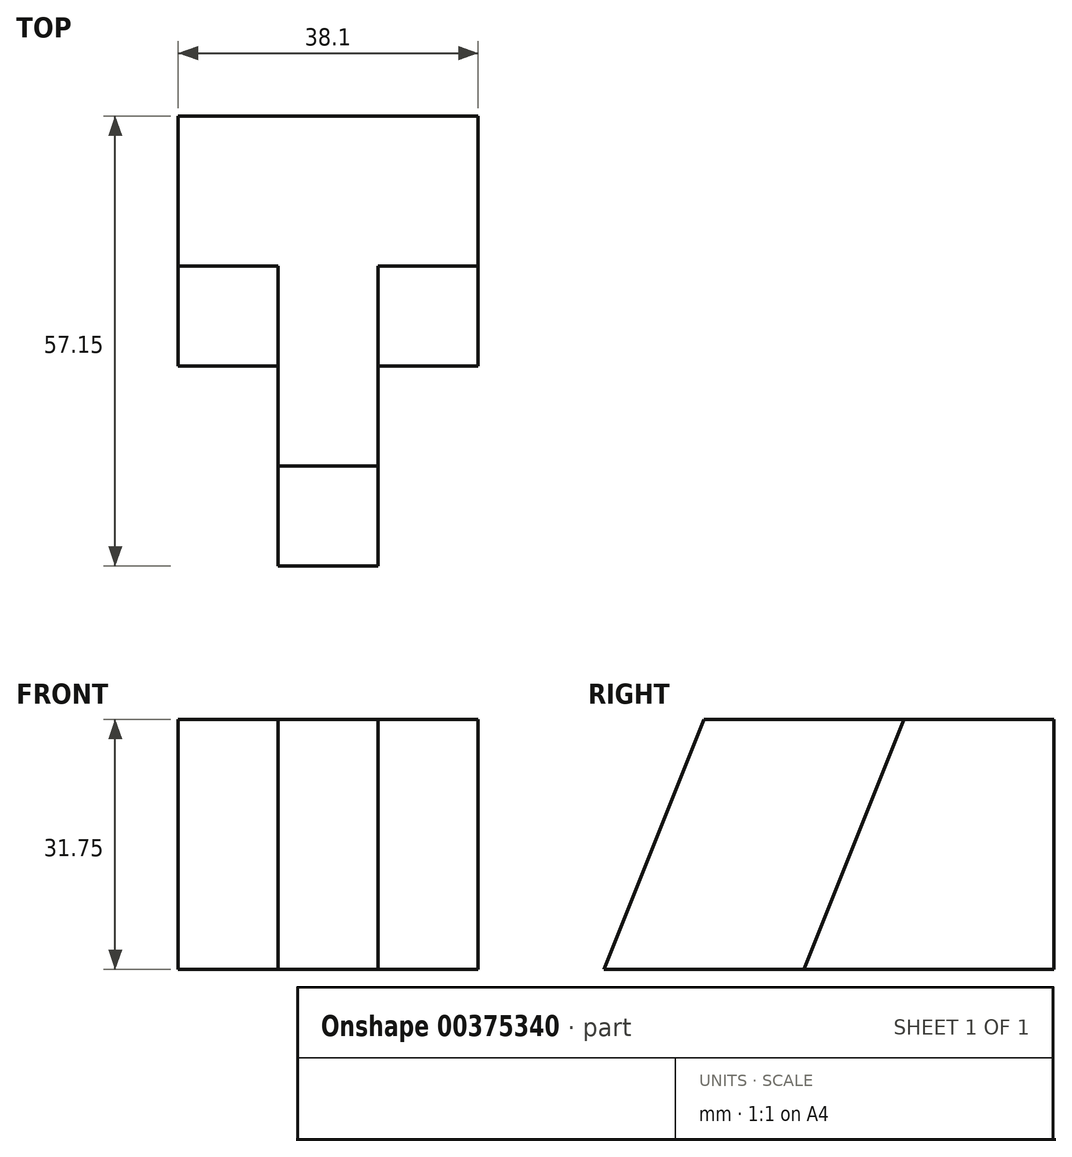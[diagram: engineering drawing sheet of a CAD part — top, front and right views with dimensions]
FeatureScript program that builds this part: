
annotation { "Feature Type Name" : "Feature", "Feature Type Description" : "" }
export const myFeature = defineFeature(function(context is Context, id is Id, definition is map)
    precondition{}
    {
        {
            var Q0;
            Q0=qCreatedBy(makeId("Top.planeOp"),FACE);
            var sketch = newSketch(context, id + "F0", { "sketchPlane" : qUnion([Q0])});
            skLineSegment(sketch, "E0", {"start": v(0, 0) * mm, "end": v(0, -19.05) * mm});
            skLineSegment(sketch, "E1", {"start": v(0, -19.05) * mm, "end": v(12.7, -19.05) * mm});
            skLineSegment(sketch, "E2", {"start": v(12.7, -19.05) * mm, "end": v(12.7, -44.45) * mm});
            skLineSegment(sketch, "E3", {"start": v(12.7, -44.45) * mm, "end": v(25.4, -44.45) * mm});
            skLineSegment(sketch, "E4", {"start": v(25.4, -44.45) * mm, "end": v(25.4, -19.05) * mm});
            skLineSegment(sketch, "E5", {"start": v(25.4, -19.05) * mm, "end": v(38.1, -19.05) * mm});
            skLineSegment(sketch, "E6", {"start": v(38.1, -19.05) * mm, "end": v(38.1, 0) * mm});
            skLineSegment(sketch, "E7", {"start": v(38.1, 0) * mm, "end": v(0, 0) * mm});
            skSolve(sketch);
        }
        {
            var Q0;
            Q0 = qSketchRegion(id + "F0", true);
            extrude(context, id + "F1", {"entities" : qUnion([Q0]), "depth" : 31.75 * mm});
        }
        {
            var Q0;
            Q0=makeQuery(id+"F1.opExtrude","SWEPT_FACE",FACE,{"disambiguationData":[OSD([sQuery(id+"F0.wireOp",EDGE,"E4")])]});
            var sketch = newSketch(context, id + "F2", { "sketchPlane" : qUnion([Q0])});
            skLineSegment(sketch, "E8", {"start": v(-19.05, 0) * mm, "end": v(-31.75, 0) * mm});
            skLineSegment(sketch, "E9", {"start": v(-31.75, 0) * mm, "end": v(-19.05, 31.75) * mm});
            skSolve(sketch);
        }
        {
            var Q0;
            Q0 = qSketchRegion(id + "F2", true);
            var Q1;
            Q1=makeQuery(id+"F2.imprint","IMPRINT",FACE,{"disambiguationData":[TD([[makeQuery(id+"F2.imprint","IMPRINT",EDGE,{"derivedFrom":sQuery(id+"F2.wireOp",EDGE,"E8")}),1.0]])]});
            extrude(context, id + "F3", {"entities" : qUnion([Q0, Q1]), "operationType" : NewBodyOperationType.ADD, "depth" : 12.7 * mm});
        }
        {
            var Q0;
            Q0=makeQuery(id+"F1.opExtrude","SWEPT_FACE",FACE,{"disambiguationData":[OSD([sQuery(id+"F0.wireOp",EDGE,"E2")])]});
            var sketch = newSketch(context, id + "F4", { "sketchPlane" : qUnion([Q0])});
            skLineSegment(sketch, "E10", {"start": v(19.05, 0) * mm, "end": v(31.75, 0) * mm});
            skLineSegment(sketch, "E11", {"start": v(31.75, 0) * mm, "end": v(19.05, 31.75) * mm});
            skSolve(sketch);
        }
        {
            var Q0;
            Q0 = qSketchRegion(id + "F4", true);
            var Q1;
            Q1=makeQuery(id+"F4.imprint","IMPRINT",FACE,{"disambiguationData":[TD([[makeQuery(id+"F4.imprint","IMPRINT",EDGE,{"derivedFrom":sQuery(id+"F4.wireOp",EDGE,"E10")}),1.0]])]});
            extrude(context, id + "F5", {"entities" : qUnion([Q0, Q1]), "operationType" : NewBodyOperationType.ADD, "depth" : 12.7 * mm});
        }
        {
            var Q0;
            Q0=makeQuery(id+"F1.opExtrude","SWEPT_FACE",FACE,{"disambiguationData":[OSD([sQuery(id+"F0.wireOp",EDGE,"E4")])]});
            var sketch = newSketch(context, id + "F6", { "sketchPlane" : qUnion([Q0])});
            skLineSegment(sketch, "E12", {"start": v(-44.45, 0) * mm, "end": v(-57.15, 0) * mm});
            skLineSegment(sketch, "E13", {"start": v(-57.15, 0) * mm, "end": v(-44.45, 31.75) * mm});
            skSolve(sketch);
        }
        {
            var Q0;
            Q0 = qSketchRegion(id + "F6", true);
            var Q1;
            Q1=makeQuery(id+"F6.imprint","IMPRINT",FACE,{"disambiguationData":[TD([[makeQuery(id+"F6.imprint","IMPRINT",EDGE,{"derivedFrom":sQuery(id+"F6.wireOp",EDGE,"E12")}),-1.0]])]});
            extrude(context, id + "F7", {"entities" : qUnion([Q0, Q1]), "operationType" : NewBodyOperationType.ADD, "oppositeDirection" : true, "depth" : 12.7 * mm});
        }
    });
